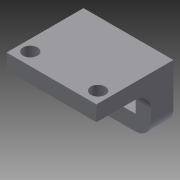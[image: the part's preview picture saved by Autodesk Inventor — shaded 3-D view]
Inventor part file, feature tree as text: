
AUTODESK INVENTOR PART (.ipt)
format: ipt  version: 2014 (Build 180170000, 170)  size: 117,248 bytes
history: native  units: in
note: dims shown in document units (in); Inventor stores cm internally (conversion verified against a paired STEP export)
features: extrude x3, sketch x3, fillet x2
ambient origin geometry x8: Origin, YZ Plane, XZ Plane, XY Plane, X Axis, Y Axis, Z Axis, Center Point
bodies: Solid1 (feature_tree)
feature tree (8):
  extrude  "Extrusion1"  Depth=0.54in
  extrude  "Extrusion2"  Depth=0.3in
  extrude  "Extrusion3"  Depth=1.0625in TaperAngle=0.0deg
  fillet  "Fillet1"  Radius=0.2812in
  fillet  "Fillet2"  Radius=0.2812in
  sketch  "Sketch1"  dims[d0=1.153in d1=0.54in]
  sketch  "Sketch2"  dims[d2=0.3in d3=0.3in]
  sketch  "Sketch3"  dims[d4=0.4375in d5=0.0in d6=1.0625in d7=0.0in d8=0.2812in d9=0.2812in d10=1.0625in d11=0.0in d12=0.3125in d13=0.3125in]
